# Revit family: Towel_Ring-American_Standard-Townsend-7455190_Series
name_source: partatom
category: Specialty Equipment
units: mm (PartAtom-declared; Revit-internal decimal feet)

## family parameters
Cut with Voids When Loaded = No
Host = Face
OmniClass Number = 23.40.20.21
OmniClass Title = Toilet and Bath Specialties
Part Type = Normal
Room Calculation Point = No
Round Connector Dimension = Use Diameter
Shared = Yes

## types (6) — shared parameters
Assembly Code = C1030220
Base = 2 3/16"
Default Elevation = 40"
Description = Town Square® S Towel Ring
Height = 8 1/4"
Installation Type = Wall Mounted
Length = 3 5/8"
Manufacturer = American Standard
Product Documentation Link = https://lixil.cdn.celum.cloud
Product Page URL = https://www.americanstandard-us.com
Revised Date = 02/26/2024
URL = http://www.americanstandard-us.com
Warranty Information = Limited Lifetime Warranty
Width = 7 3/8"

## per-type parameters (varying)
| type | Finish | Material |
| 7455190.002 | Metal-American Standard-002-Polished Chrome | Metal-American Standard-002-Polished Chrome |
| 7455190.GN0 | Metal-American Standard-GN0-Brushed Cool Sunrise | Metal-American Standard-GN0-Brushed Cool Sunrise |
| 7455190.243 | Metal-American Standard-243-Matte Black | Metal-American Standard-243-Matte Black |
| 7455190.295 | Metal-American Standard-295-Brushed Nickel | Metal-American Standard-295-Brushed Nickel |
| 7455190.278 | Metal-American Standard-278-Legacy Bronze | Metal-American Standard-278-Legacy Bronze |
| 7455190.013 | Metal-American Standard-013-Polished Nickel | Metal-American Standard-013-Polished Nickel |

note: column(s) folded — value = type name in every type: Model

## geometry (parser evidence)
native form markers: Sweep x3
no freeform markers — native parametric forms only
